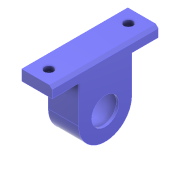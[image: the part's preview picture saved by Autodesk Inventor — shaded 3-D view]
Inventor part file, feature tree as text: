
AUTODESK INVENTOR PART (.ipt)
format: ipt  version: 2022 (Build 260153000, 153)  size: 173,056 bytes
history: native  units: mm
features: sketch x5, projected_geometry x4, extrude x3, hole x2, chamfer x2, thicken_offset x1
ambient origin geometry x8: Origin, YZ Plane, XZ Plane, XY Plane, X Axis, Y Axis, Z Axis, Center Point
bodies: Solid1 (feature_tree)
feature tree (17):
  extrude  "Extrusion1"  Depth=14.0mm
  extrude  "Extrusion2"  Depth=4.0mm TaperAngle=0.0deg
  hole  "Hole1"  [1 undecoded]
  hole  "Hole3"  [1 undecoded]
  thicken_offset  "Thicken1"
  extrude  "Extrusion3"  Depth=5.0mm
  chamfer  "Chamfer2"  Distance=0.15mm
  chamfer  "Chamfer3"  Distance=1.5mm
  sketch  "Sketch1"  dims[d2=20.0mm d1=14.0mm]
  sketch  "Sketch2"  dims[d3=0.0mm d5=4.0mm d6=0.0mm]
  sketch  "Sketch3"  dims[d7=3.4mm d8=6.0mm d9=6.0mm d10=2.0mm d11=90.0deg d12=8.0mm d13=20.594885mm d21=13.0mm]
  sketch  "Sketch5"  dims[d22=6.0mm d23=4.0mm d24=2.0mm d25=90.0deg d26=8.0mm d27=20.594885mm d28=40.0mm]
  sketch  "Sketch6"  dims[d30=5.0mm d31=5.0mm d32=0.15mm d33=0.15mm d37=1.5mm d38=1.0mm d39=0.0mm d40=0.5mm d41=2.0mm d42=45.0deg d43=1.0mm d44=2.0mm d45=45.0deg d46=0.5mm d47=0.872665mm d48=0.5mm d49=0.872665mm]
  projected_geometry  "Project Cut Edges1"
  projected_geometry  "Project Cut Edges2"
  projected_geometry  "Project Cut Edges3"
  projected_geometry  "Project Cut Edges4"
note: 2 required parameter values undecoded (feature->parameter linkage not recoverable at this tier; creation-order binding heuristic only, values carry confidence <= 0.55)
